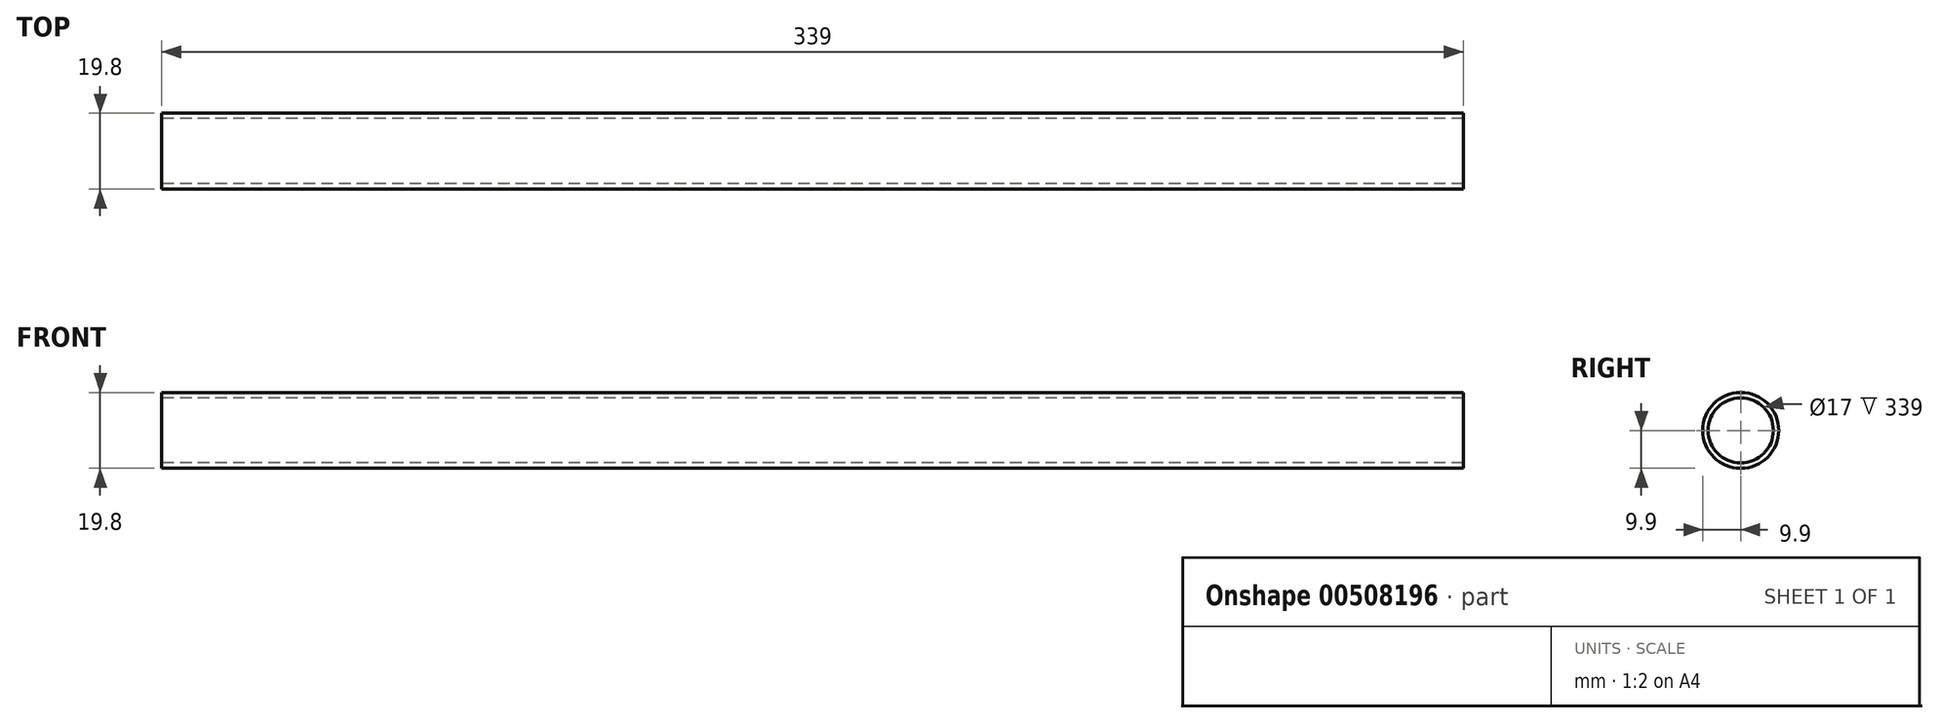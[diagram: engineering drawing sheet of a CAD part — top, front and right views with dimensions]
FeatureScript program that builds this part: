
annotation { "Feature Type Name" : "Feature", "Feature Type Description" : "" }
export const myFeature = defineFeature(function(context is Context, id is Id, definition is map)
    precondition{}
    {
        {
            var Q0;
            Q0=qCreatedBy(makeId("Right.planeOp"),FACE);
            var sketch = newSketch(context, id + "F0", { "sketchPlane" : qUnion([Q0])});
            skCircle(sketch, "E0", {"center": v(0, 0) * mm, "radius": 8.5 * mm});
            skCircle(sketch, "E1", {"center": v(0, 0) * mm, "radius": 9.9 * mm});
            skSolve(sketch);
        }
        {
            var Q0;
            Q0 = qSketchRegion(id + "F0", true);
            extrude(context, id + "F1", {"entities" : qUnion([Q0]), "depth" : 339 * mm, "offsetDistance" : 25 * mm});
        }
    });
